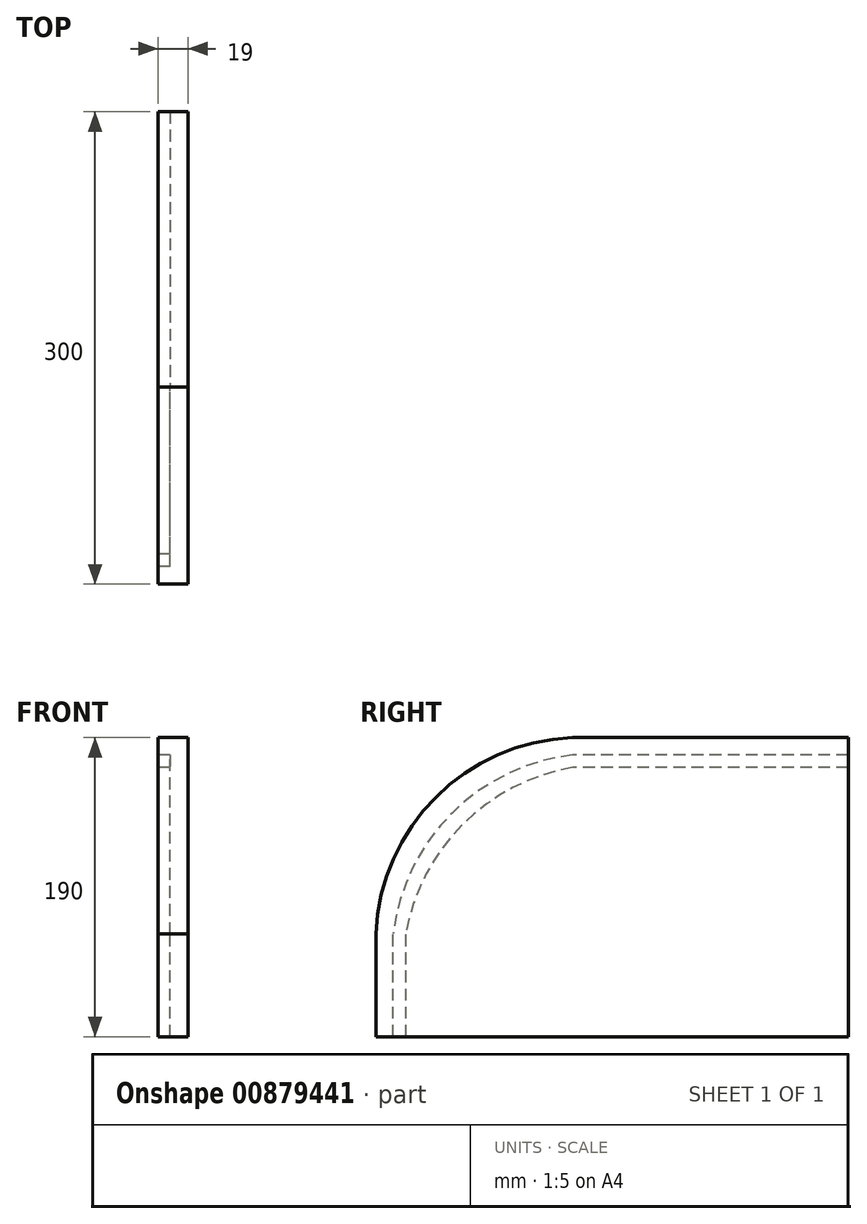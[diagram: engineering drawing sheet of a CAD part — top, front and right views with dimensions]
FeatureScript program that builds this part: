
annotation { "Feature Type Name" : "Feature", "Feature Type Description" : "" }
export const myFeature = defineFeature(function(context is Context, id is Id, definition is map)
    precondition{}
    {
        {
            var Q0;
            Q0=qCreatedBy(makeId("Right.planeOp"),FACE);
            var sketch = newSketch(context, id + "F0", { "sketchPlane" : qUnion([Q0])});
            skLineSegment(sketch, "E0.bottom", {"start": v(-25, 95) * mm, "end": v(150, 95) * mm});
            skLineSegment(sketch, "E0.top", {"start": v(-150, -95) * mm, "end": v(150, -95) * mm});
            skLineSegment(sketch, "E0.left", {"start": v(-150, -29.82) * mm, "end": v(-150, -95) * mm});
            skLineSegment(sketch, "E0.right", {"start": v(150, 95) * mm, "end": v(150, -95) * mm});
            skPoint(sketch, "E0.middle", {"position": v(0, 0) * mm});
            skPoint(sketch, "E1", {"position": v(-150, -40) * mm});
            skPoint(sketch, "E2", {"position": v(-25, 95) * mm});
            skArc(sketch, "E3", {"start": v(-25, 95) * mm, "mid": v(-115.49, 53.42) * mm, "end": v(-150, -40) * mm});
            skPoint(sketch, "E4.orphan", {"position": v(-150, 95) * mm});
            skSolve(sketch);
        }
        {
            var Q0;
            {var subQ5=sQuery(id+"F0.wireOp",EDGE,"E0.bottom");Q0=makeQuery(id+"F0.imprint","IMPRINT",FACE,{"disambiguationData":[TD([[makeQuery(id+"F0.imprint","IMPRINT",EDGE,{"derivedFrom":subQ5}),-1.0]])]});}
            extrude(context, id + "F1", {"entities" : qUnion([Q0]), "flatOperationType" : FlatOperationType.REMOVE, "depth" : 19 * mm, "offsetDistance" : 25 * mm, "domain" : OperationDomain.MODEL});
        }
        {
            var Q0;
            Q0=makeQuery(id+"F1.opExtrude","CAP_FACE",FACE,{"disambiguationData":[OSD([sQuery(id+"F0.wireOp",EDGE,"E0.bottom"),sQuery(id+"F0.wireOp",EDGE,"E0.top"),sQuery(id+"F0.wireOp",EDGE,"E0.left"),sQuery(id+"F0.wireOp",EDGE,"E0.right"),sQuery(id+"F0.wireOp",EDGE,"E3")])],"isStart":true});
            var sketch = newSketch(context, id + "F2", { "sketchPlane" : qUnion([Q0])});
            skPoint(sketch, "E5", {"position": v(-150, 84) * mm});
            skLineSegment(sketch, "E6", {"start": v(-150, 84) * mm, "end": v(25, 84) * mm});
            skPoint(sketch, "E7", {"position": v(-150, 76) * mm});
            skLineSegment(sketch, "E8", {"start": v(-150, 76) * mm, "end": v(25, 76) * mm});
            skPoint(sketch, "E9", {"position": v(139, -95) * mm});
            skPoint(sketch, "E10", {"position": v(131, -95) * mm});
            skLineSegment(sketch, "E11", {"start": v(139, -95) * mm, "end": v(139, -29.82) * mm});
            skLineSegment(sketch, "E12", {"start": v(131, -95) * mm, "end": v(131, -29.82) * mm});
            skArc(sketch, "E13", {"start": v(139, -29.82) * mm, "mid": v(101.75, 46.88) * mm, "end": v(25, 84) * mm});
            skArc(sketch, "E14", {"start": v(131, -29.82) * mm, "mid": v(94.77, 39.9) * mm, "end": v(25, 76) * mm});
            skSolve(sketch);
        }
        {
            var Q0;
            {var subQ1=sQuery(id+"F2.wireOp",EDGE,"E6");Q0=makeQuery(id+"F2.imprint","IMPRINT",FACE,{"disambiguationData":[TD([[makeQuery(id+"F2.imprint","IMPRINT",EDGE,{"derivedFrom":subQ1}),-1.0]])]});}
            extrude(context, id + "F3", {"entities" : qUnion([Q0]), "operationType" : NewBodyOperationType.REMOVE, "flatOperationType" : FlatOperationType.REMOVE, "oppositeDirection" : true, "depth" : 7.5 * mm, "offsetDistance" : 25 * mm, "domain" : OperationDomain.MODEL});
        }
    });
